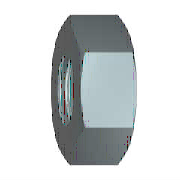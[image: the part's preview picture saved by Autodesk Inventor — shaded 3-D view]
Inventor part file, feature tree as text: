
AUTODESK INVENTOR PART (.ipt)
format: ipt  version: 2023 (Build 270158000, 158)  size: 164,352 bytes
history: native  units: mm (DEFAULTED — no unit token found)
features: sketch x3, other x2, extrude x1, hole x1, plane x1
ambient origin geometry x7: Origin, YZ Plane, XZ Plane, X Axis, Y Axis, Z Axis, Center Point
bodies: Solid1 (feature_tree)
feature tree (8):
  extrude  "Базовый элемент"  Depth=27.712813mm
  other  "Фаска1"
  hole  "Резьба"  [1 undecoded]
  other  "Work Axis1"
  plane  "Work Plane1"
  sketch  "Эскиз1"
  sketch  "Эскиз2"
  sketch  "Эскиз3"
note: 1 required parameter value undecoded (feature->parameter linkage not recoverable at this tier; creation-order binding heuristic only, values carry confidence <= 0.55)
